# Revit family: NBS_DudleyIndustriesLimited_HandDryers_ModuloHandDryer
name_source: partatom
category: Electrical Fixtures
revit_build: Autodesk Revit 2017 (Build: 20171027_0315(x64)
units: mm (PartAtom-declared; Revit-internal decimal feet)

## family parameters
Always vertical = No
Cut with Voids When Loaded = No
Maintain Annotation Orientation = No
Part Type = Normal
Room Calculation Point = No
Round Connector Dimension = Use Diameter
Shared = No
Work Plane-Based = No

## types (1)
- ModuloHandDryer
    AirVolume = 130 m³/h
    AssetType = Fixed
    BIMObjectName = NBS_DudleyIndustriesLimited_HandDryers_ModuloHandDryer
    BodyIngressProtection = IP21
    Category = Pr_40_70_62_37:Hand driers
    CodePerformance = CE BS EN 60335-2-23:2003 + A1:2008 (Particular Requirements for Appliances for skin and hair Care) and BS EN60335-1:2002 + A2:2006 (incorporating A1,A11,A12, A13), (Safety of Household and similar electrical appliances), EN55014-1: 2006 + A1: 2009, EN55014-2: 1997 + A1: 2001 + A2:2008, EN61000-3-2: 2006, EN61000-3-3: 2008, RoHS, WEEE
    Color = Black
    Description = Automatic, energy efficient hand dryer
    DurationUnit = year
    ElectricalSupplyFrequency = 0 mm  [stored 0 ft]
    ElectricalSupplyPowerRating = 1.7kW @230 volts
    ElectricalSupplyRatedOperationalVoltageUe = 230 V ac
    ExpectedLife = 5
    Features = Fits the modulo behind the mirror system, provides a hygienic, comfortable and fast hand drying solution, produces no waste, no requirement to re-stock, quiet operation at just 71 dBA, simple to install, utilises a full modular cabinet space, blanking plates available separately if required
    Finish = Matte black powder coated
    Form = High performance warm air hand dryer
    HandDryerBodyMaterial = NBS_Concept
    IfcExportAs = IfcElectricApplianceType
    IfcExportType = HANDDRYER
    IsBuiltIn = Yes
    ManufacturerName = Dudley Industries Limited
    ManufacturerURL = https://www.dudleyindustries.com
    Material = Cover and back plate: CR1 CS2 steel, base plate: 1.4509 stainless steel
    ModelNumber = 92372BK
    ModelReference = Modulo Hand Dryer
    NBSCertification = www.nationalbimlibrary.com/cert/weoy1555
    NBSDescription = Hand dryers
    NBSReference = 45-35-72/334
    Name = HandDryers_ModuloHandDryer_DudleyIndustriesLimited
    NoiseLevelAt1M = 71 dBA
    NominalDepth = 193 mm
    NominalHeight = 330 mm  [stored 1.08268 ft]
    NominalLength = 388 mm  [stored 1.27297 ft]
    NominalWidth = 0 mm  [stored 0 ft]
    Operation = Automatic start/stop
    PackingCarton = 1 piece
    SensorRange = 100 mm
    Size = 388 x 330 x 193 mm
    Status = UNSET
    Style = Hand dryer
    Uniclass2015Code = Pr_40_70_62_37
    Uniclass2015Title = Hand driers
    Uniclass2015Version = Products v1.12
    Version = 1
    WarrantyDescription = 5 years
    WarrantyDurationUnit = year
    Weight = 6.5 kg

note: [stored X ft] marks values corroborated as IEEE doubles in the binary element streams (Revit-internal decimal feet)

## geometry (parser evidence)
native form markers: Sweep x1
no freeform markers — native parametric forms only
